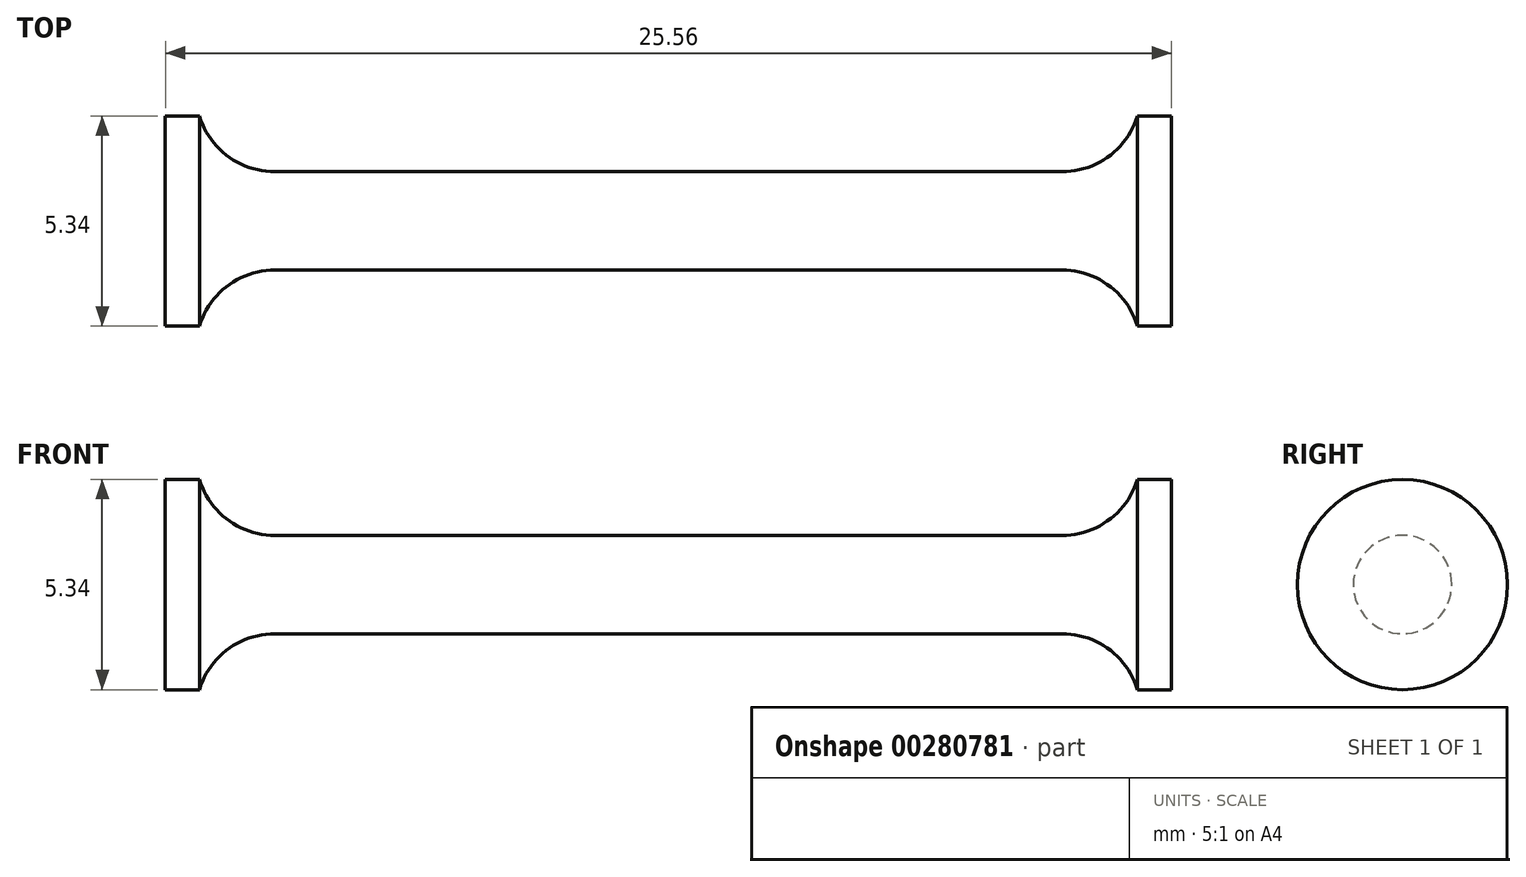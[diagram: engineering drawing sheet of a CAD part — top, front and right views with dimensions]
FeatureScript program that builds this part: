
annotation { "Feature Type Name" : "Feature", "Feature Type Description" : "" }
export const myFeature = defineFeature(function(context is Context, id is Id, definition is map)
    precondition{}
    {
        {
            var Q0;
            Q0=qCreatedBy(makeId("Front.planeOp"),FACE);
            var sketch = newSketch(context, id + "F0", { "sketchPlane" : qUnion([Q0])});
            skLineSegment(sketch, "E0", {"start": v(0, 1.25) * mm, "end": v(10, 1.25) * mm});
            skArc(sketch, "E1", {"start": v(10, 1.25) * mm, "mid": v(11.2, 1.64) * mm, "end": v(11.91, 2.67) * mm});
            skLineSegment(sketch, "E2", {"start": v(11.91, 2.67) * mm, "end": v(12.78, 2.67) * mm});
            skLineSegment(sketch, "E3", {"start": v(12.78, 2.67) * mm, "end": v(12.78, 0) * mm});
            skLineSegment(sketch, "E4.MirrorCS", {"start": v(0, 1.25) * mm, "end": v(-10, 1.25) * mm});
            skLineSegment(sketch, "E5.MirrorCS", {"start": v(-12.78, 2.67) * mm, "end": v(-12.78, 0) * mm});
            skLineSegment(sketch, "E6.MirrorCS", {"start": v(-11.91, 2.67) * mm, "end": v(-12.78, 2.67) * mm});
            skArc(sketch, "E7.MirrorCS", {"start": v(-10, 1.25) * mm, "mid": v(-11.2, 1.64) * mm, "end": v(-11.91, 2.67) * mm});
            skLineSegment(sketch, "E8", {"start": v(-12.78, 0) * mm, "end": v(12.78, 0) * mm});
            skSolve(sketch);
        }
        {
            var Q0;
            Q0=makeQuery(id+"F0.imprint","IMPRINT",FACE,{"disambiguationData":[TD([[makeQuery(id+"F0.imprint","IMPRINT",EDGE,{"derivedFrom":sQuery(id+"F0.wireOp",EDGE,"E0")}),-1.0]])]});
            var Q1;
            Q1=sQuery(id+"F0.wireOp",EDGE,"E8");
            revolve(context, id + "F1", {"entities" : qUnion([Q0]), "axis" : qUnion([Q1]), "revolveType" : RevolveType.FULL});
        }
    });
